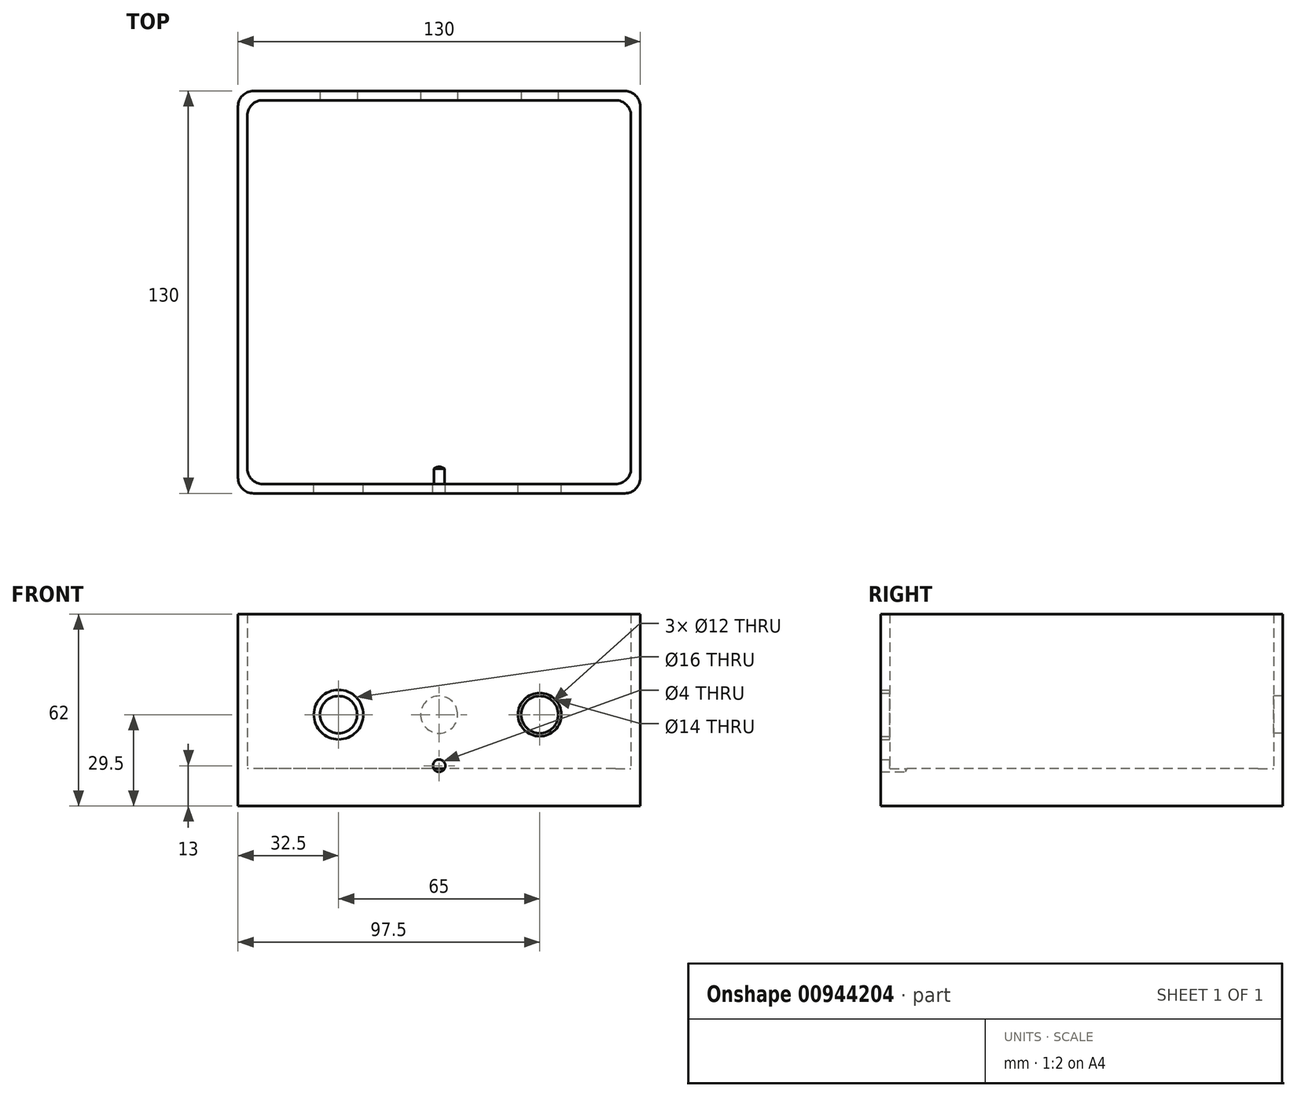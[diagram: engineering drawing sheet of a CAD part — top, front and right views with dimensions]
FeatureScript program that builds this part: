
annotation { "Feature Type Name" : "Feature", "Feature Type Description" : "" }
export const myFeature = defineFeature(function(context is Context, id is Id, definition is map)
    precondition{}
    {
        {
            var Q0;
            Q0=qCreatedBy(makeId("Top.planeOp"),FACE);
            var sketch = newSketch(context, id + "F0", { "sketchPlane" : qUnion([Q0])});
            skLineSegment(sketch, "E0.bottom", {"start": v(60, 65) * mm, "end": v(-60, 65) * mm});
            skLineSegment(sketch, "E0.top", {"start": v(60, -65) * mm, "end": v(-60, -65) * mm});
            skLineSegment(sketch, "E0.left", {"start": v(65, 60) * mm, "end": v(65, -60) * mm});
            skLineSegment(sketch, "E0.right", {"start": v(-65, 60) * mm, "end": v(-65, -60) * mm});
            skPoint(sketch, "E0.middle", {"position": v(0, 0) * mm});
            skLineSegment(sketch, "E1.bottom", {"start": v(57, 62) * mm, "end": v(-57, 62) * mm});
            skLineSegment(sketch, "E1.top", {"start": v(57, -62) * mm, "end": v(-57, -62) * mm});
            skLineSegment(sketch, "E1.left", {"start": v(62, 57) * mm, "end": v(62, -57) * mm});
            skLineSegment(sketch, "E1.right", {"start": v(-62, 57) * mm, "end": v(-62, -57) * mm});
            skPoint(sketch, "E2.visualSharp", {"position": v(-65, 65) * mm});
            skArc(sketch, "E2.filletArc", {"start": v(-60, 65) * mm, "mid": v(-63.54, 63.54) * mm, "end": v(-65, 60) * mm});
            skPoint(sketch, "E3.visualSharp", {"position": v(-65, -65) * mm});
            skArc(sketch, "E3.filletArc", {"start": v(-65, -60) * mm, "mid": v(-63.54, -63.54) * mm, "end": v(-60, -65) * mm});
            skPoint(sketch, "E4.visualSharp", {"position": v(65, -65) * mm});
            skArc(sketch, "E4.filletArc", {"start": v(60, -65) * mm, "mid": v(63.54, -63.54) * mm, "end": v(65, -60) * mm});
            skPoint(sketch, "E5.visualSharp", {"position": v(65, 65) * mm});
            skArc(sketch, "E5.filletArc", {"start": v(65, 60) * mm, "mid": v(63.54, 63.54) * mm, "end": v(60, 65) * mm});
            skPoint(sketch, "E6.visualSharp", {"position": v(-62, -62) * mm});
            skArc(sketch, "E6.filletArc", {"start": v(-62, -57) * mm, "mid": v(-60.54, -60.54) * mm, "end": v(-57, -62) * mm});
            skPoint(sketch, "E7.visualSharp", {"position": v(62, 62) * mm});
            skArc(sketch, "E7.filletArc", {"start": v(62, 57) * mm, "mid": v(60.54, 60.54) * mm, "end": v(57, 62) * mm});
            skPoint(sketch, "E8.visualSharp", {"position": v(62, -62) * mm});
            skArc(sketch, "E8.filletArc", {"start": v(57, -62) * mm, "mid": v(60.54, -60.54) * mm, "end": v(62, -57) * mm});
            skPoint(sketch, "E9.visualSharp", {"position": v(-62, 62) * mm});
            skArc(sketch, "E9.filletArc", {"start": v(-57, 62) * mm, "mid": v(-60.54, 60.54) * mm, "end": v(-62, 57) * mm});
            skSolve(sketch);
        }
        {
            var Q0;
            Q0=makeQuery(id+"F0.imprint","IMPRINT",FACE,{"disambiguationData":[TD([[makeQuery(id+"F0.imprint","IMPRINT",EDGE,{"derivedFrom":sQuery(id+"F0.wireOp",EDGE,"E0.bottom")}),1.0]])]});
            extrude(context, id + "F1", {"entities" : qUnion([Q0]), "flatOperationType" : FlatOperationType.REMOVE, "depth" : 62 * mm, "offsetDistance" : 25 * mm, "domain" : OperationDomain.MODEL});
        }
        {
            var Q0;
            Q0=makeQuery(id+"F0.imprint","IMPRINT",FACE,{"disambiguationData":[TD([[makeQuery(id+"F0.imprint","IMPRINT",EDGE,{"derivedFrom":sQuery(id+"F0.wireOp",EDGE,"E1.bottom")}),1.0]])]});
            extrude(context, id + "F2", {"entities" : qUnion([Q0]), "operationType" : NewBodyOperationType.ADD, "depth" : 12 * mm, "offsetDistance" : 25 * mm});
        }
        {
            var Q0;
            Q0=makeQuery(id+"F1.opExtrude","SWEPT_FACE",FACE,{"disambiguationData":[OSD([sQuery(id+"F0.wireOp",EDGE,"E0.bottom")])]});
            var sketch = newSketch(context, id + "F3", { "sketchPlane" : qUnion([Q0])});
            skPoint(sketch, "E10", {"position": v(-32.5, 29.5) * mm});
            skPoint(sketch, "E11", {"position": v(0, 29.5) * mm});
            skPoint(sketch, "E12", {"position": v(32.5, 29.5) * mm});
            skCircle(sketch, "E13", {"center": v(-32.5, 29.5) * mm, "radius": 6 * mm});
            skCircle(sketch, "E14", {"center": v(0, 29.5) * mm, "radius": 6 * mm});
            skCircle(sketch, "E15", {"center": v(32.5, 29.5) * mm, "radius": 6 * mm});
            skSolve(sketch);
        }
        {
            var Q0;
            Q0=sQuery(id+"F3.wireOp",VERTEX,"E10");
            var Q1;
            Q1=sQuery(id+"F3.wireOp",VERTEX,"E11");
            var Q2;
            Q2=sQuery(id+"F3.wireOp",VERTEX,"E12");
            var Q3;
            Q3=makeQuery(id+"F1.opExtrude","SWEPT_BODY",BODY,{"disambiguationData":[OSD([sQuery(id+"F0.wireOp",EDGE,"E0.bottom"),sQuery(id+"F0.wireOp",EDGE,"E0.top"),sQuery(id+"F0.wireOp",EDGE,"E0.left"),sQuery(id+"F0.wireOp",EDGE,"E0.right"),sQuery(id+"F0.wireOp",EDGE,"E1.bottom"),sQuery(id+"F0.wireOp",EDGE,"E1.top"),sQuery(id+"F0.wireOp",EDGE,"E1.left"),sQuery(id+"F0.wireOp",EDGE,"E1.right"),sQuery(id+"F0.wireOp",EDGE,"E2.filletArc"),sQuery(id+"F0.wireOp",EDGE,"E3.filletArc"),sQuery(id+"F0.wireOp",EDGE,"E4.filletArc"),sQuery(id+"F0.wireOp",EDGE,"E5.filletArc"),sQuery(id+"F0.wireOp",EDGE,"E6.filletArc"),sQuery(id+"F0.wireOp",EDGE,"E7.filletArc"),sQuery(id+"F0.wireOp",EDGE,"E8.filletArc"),sQuery(id+"F0.wireOp",EDGE,"E9.filletArc")])]});
            hole(context, id + "F4", {"style" : HoleStyle.SIMPLE, "endStyle" : HoleEndStyle.BLIND, "holeDiameter" : 12 * mm, "majorDiameter" : 5 * mm, "holeDepth" : 8 * mm, "isTappedThrough" : true, "tappedDepth" : 12 * mm, "tapClearance" : 3, "locations" : qUnion([Q0, Q1, Q2]), "scope" : qUnion([Q3]), "startStyle" : HoleStartStyle.PART});
        }
        {
            var Q0;
            Q0=makeQuery(id+"F1.opExtrude","SWEPT_FACE",FACE,{"disambiguationData":[OSD([sQuery(id+"F0.wireOp",EDGE,"E0.top")])]});
            var sketch = newSketch(context, id + "F5", { "sketchPlane" : qUnion([Q0])});
            skPoint(sketch, "E16", {"position": v(-32.5, 29.5) * mm});
            skPoint(sketch, "E17", {"position": v(0, 13) * mm});
            skPoint(sketch, "E18", {"position": v(32.5, 29.5) * mm});
            skCircle(sketch, "E19", {"center": v(-32.5, 29.5) * mm, "radius": 8 * mm});
            skCircle(sketch, "E20", {"center": v(32.5, 29.5) * mm, "radius": 7 * mm});
            skCircle(sketch, "E21", {"center": v(0, 13) * mm, "radius": 2 * mm});
            skSolve(sketch);
        }
        {
            var Q0;
            Q0=sQuery(id+"F5.wireOp",VERTEX,"E16");
            var Q1;
            Q1=makeQuery(id+"F1.opExtrude","SWEPT_BODY",BODY,{"disambiguationData":[OSD([sQuery(id+"F0.wireOp",EDGE,"E0.bottom"),sQuery(id+"F0.wireOp",EDGE,"E0.top"),sQuery(id+"F0.wireOp",EDGE,"E0.left"),sQuery(id+"F0.wireOp",EDGE,"E0.right"),sQuery(id+"F0.wireOp",EDGE,"E1.bottom"),sQuery(id+"F0.wireOp",EDGE,"E1.top"),sQuery(id+"F0.wireOp",EDGE,"E1.left"),sQuery(id+"F0.wireOp",EDGE,"E1.right"),sQuery(id+"F0.wireOp",EDGE,"E2.filletArc"),sQuery(id+"F0.wireOp",EDGE,"E3.filletArc"),sQuery(id+"F0.wireOp",EDGE,"E4.filletArc"),sQuery(id+"F0.wireOp",EDGE,"E5.filletArc"),sQuery(id+"F0.wireOp",EDGE,"E6.filletArc"),sQuery(id+"F0.wireOp",EDGE,"E7.filletArc"),sQuery(id+"F0.wireOp",EDGE,"E8.filletArc"),sQuery(id+"F0.wireOp",EDGE,"E9.filletArc")])]});
            hole(context, id + "F6", {"style" : HoleStyle.SIMPLE, "endStyle" : HoleEndStyle.BLIND, "holeDiameter" : 16 * mm, "majorDiameter" : 5 * mm, "holeDepth" : 8 * mm, "isTappedThrough" : true, "tappedDepth" : 12 * mm, "tapClearance" : 3, "locations" : qUnion([Q0]), "scope" : qUnion([Q1]), "startStyle" : HoleStartStyle.PART});
        }
        {
            var Q0;
            Q0=sQuery(id+"F5.wireOp",VERTEX,"E17");
            var Q1;
            Q1=makeQuery(id+"F1.opExtrude","SWEPT_BODY",BODY,{"disambiguationData":[OSD([sQuery(id+"F0.wireOp",EDGE,"E0.bottom"),sQuery(id+"F0.wireOp",EDGE,"E0.top"),sQuery(id+"F0.wireOp",EDGE,"E0.left"),sQuery(id+"F0.wireOp",EDGE,"E0.right"),sQuery(id+"F0.wireOp",EDGE,"E1.bottom"),sQuery(id+"F0.wireOp",EDGE,"E1.top"),sQuery(id+"F0.wireOp",EDGE,"E1.left"),sQuery(id+"F0.wireOp",EDGE,"E1.right"),sQuery(id+"F0.wireOp",EDGE,"E2.filletArc"),sQuery(id+"F0.wireOp",EDGE,"E3.filletArc"),sQuery(id+"F0.wireOp",EDGE,"E4.filletArc"),sQuery(id+"F0.wireOp",EDGE,"E5.filletArc"),sQuery(id+"F0.wireOp",EDGE,"E6.filletArc"),sQuery(id+"F0.wireOp",EDGE,"E7.filletArc"),sQuery(id+"F0.wireOp",EDGE,"E8.filletArc"),sQuery(id+"F0.wireOp",EDGE,"E9.filletArc")])]});
            hole(context, id + "F7", {"style" : HoleStyle.SIMPLE, "endStyle" : HoleEndStyle.BLIND, "holeDiameter" : 4 * mm, "majorDiameter" : 5 * mm, "holeDepth" : 8 * mm, "isTappedThrough" : true, "tappedDepth" : 12 * mm, "tapClearance" : 3, "locations" : qUnion([Q0]), "scope" : qUnion([Q1]), "startStyle" : HoleStartStyle.PART});
        }
        {
            var Q0;
            Q0=sQuery(id+"F5.wireOp",VERTEX,"E18");
            var Q1;
            Q1=makeQuery(id+"F1.opExtrude","SWEPT_BODY",BODY,{"disambiguationData":[OSD([sQuery(id+"F0.wireOp",EDGE,"E0.bottom"),sQuery(id+"F0.wireOp",EDGE,"E0.top"),sQuery(id+"F0.wireOp",EDGE,"E0.left"),sQuery(id+"F0.wireOp",EDGE,"E0.right"),sQuery(id+"F0.wireOp",EDGE,"E1.bottom"),sQuery(id+"F0.wireOp",EDGE,"E1.top"),sQuery(id+"F0.wireOp",EDGE,"E1.left"),sQuery(id+"F0.wireOp",EDGE,"E1.right"),sQuery(id+"F0.wireOp",EDGE,"E2.filletArc"),sQuery(id+"F0.wireOp",EDGE,"E3.filletArc"),sQuery(id+"F0.wireOp",EDGE,"E4.filletArc"),sQuery(id+"F0.wireOp",EDGE,"E5.filletArc"),sQuery(id+"F0.wireOp",EDGE,"E6.filletArc"),sQuery(id+"F0.wireOp",EDGE,"E7.filletArc"),sQuery(id+"F0.wireOp",EDGE,"E8.filletArc"),sQuery(id+"F0.wireOp",EDGE,"E9.filletArc")])]});
            hole(context, id + "F8", {"style" : HoleStyle.SIMPLE, "endStyle" : HoleEndStyle.BLIND, "holeDiameter" : 14 * mm, "majorDiameter" : 5 * mm, "holeDepth" : 8 * mm, "isTappedThrough" : true, "tappedDepth" : 12 * mm, "tapClearance" : 3, "locations" : qUnion([Q0]), "scope" : qUnion([Q1]), "startStyle" : HoleStartStyle.PART});
        }
    });
